# Revit family: 63__LF_UN_EmiLux_Superior_Extreme Wide_R17
name_source: partatom
category: Lighting Fixtures
revit_build: Autodesk Revit 2017 (Build: 20190508_0315(x64)
units: mm (PartAtom-declared; Revit-internal decimal feet)

## family parameters
Always vertical = Yes
Cut with Voids When Loaded = Yes
Light Source = No
Part Type = Normal
Room Calculation Point = No
Round Connector Dimension = Use Diameter
Shared = No
Work Plane-Based = No

## types (9) — shared parameters
Assembly Code = 63.0
Fixture_Material = UHMW, White
IfcExportAs = IfcLightFixtureType
IfcExportType = POINTSOURCE
Lamp = LED
Length = 1482 mm  [stored 4.8622 ft]
Manufacturer = EMILUX
Model = Superior
URL = https://emilux.nl
zero-valued in all types: Cost

## per-type parameters (varying)
| type | Apparent Load | Article Number | Dim / Dali | Emergency Lighting | Light Output | Wattage Comments |
| 6300 Lm 4000K 43W | 43 VA | 7SEW43840 | No | No | Light Output Extra Wide : 43 Watt | 43W |
| 8450 Lm 4000K 60W | 60 VA | 7SEW60840 | No | No | Light Output Extra Wide : 43 Watt | 60W |
| 10550 Lm 4000K 80W | 80 VA | 7SEW43840 | No | No | Light Output Extra Wide : 43 Watt | 80W |
| 16250 Lm 4000K 118W | 118 VA | 7SEW118840 | No | No | Light Output Extra Wide : 43 Watt | 1118W |
| 6300 Lm 4000K 43W Dim Dali | 43 VA | 33D7SDEW43840 | Yes | No | Light Output Extra Wide : 43 Watt | 43W |
| 8450 Lm 4000K 60W Dim Dali | 60 VA | 33D7SDEW60840 | Yes | No | Light Output Extra Wide : 43 Watt | 60W |
| 10550 Lm 4000K 80W Dim Dali | 80 VA | 33D7SDEW43840 | Yes | No | Light Output Extra Wide : 43 Watt | 80W |
| 16250 Lm 4000K 118W Dim Dali | 118 VA | 33D7SDEW118840 | Yes | No | Light Output Extra Wide : 43 Watt | 118W |
| 6300 Lm 4000K 43W - NV | 43 VA | 7SME43840 | No | Yes | Light Output Extra Wide : 43 Watt - NV | 43W |

note: [stored X ft] marks values corroborated as IEEE doubles in the binary element streams (Revit-internal decimal feet)

## geometry (parser evidence)
native form markers: Sweep x11
no freeform markers — native parametric forms only
